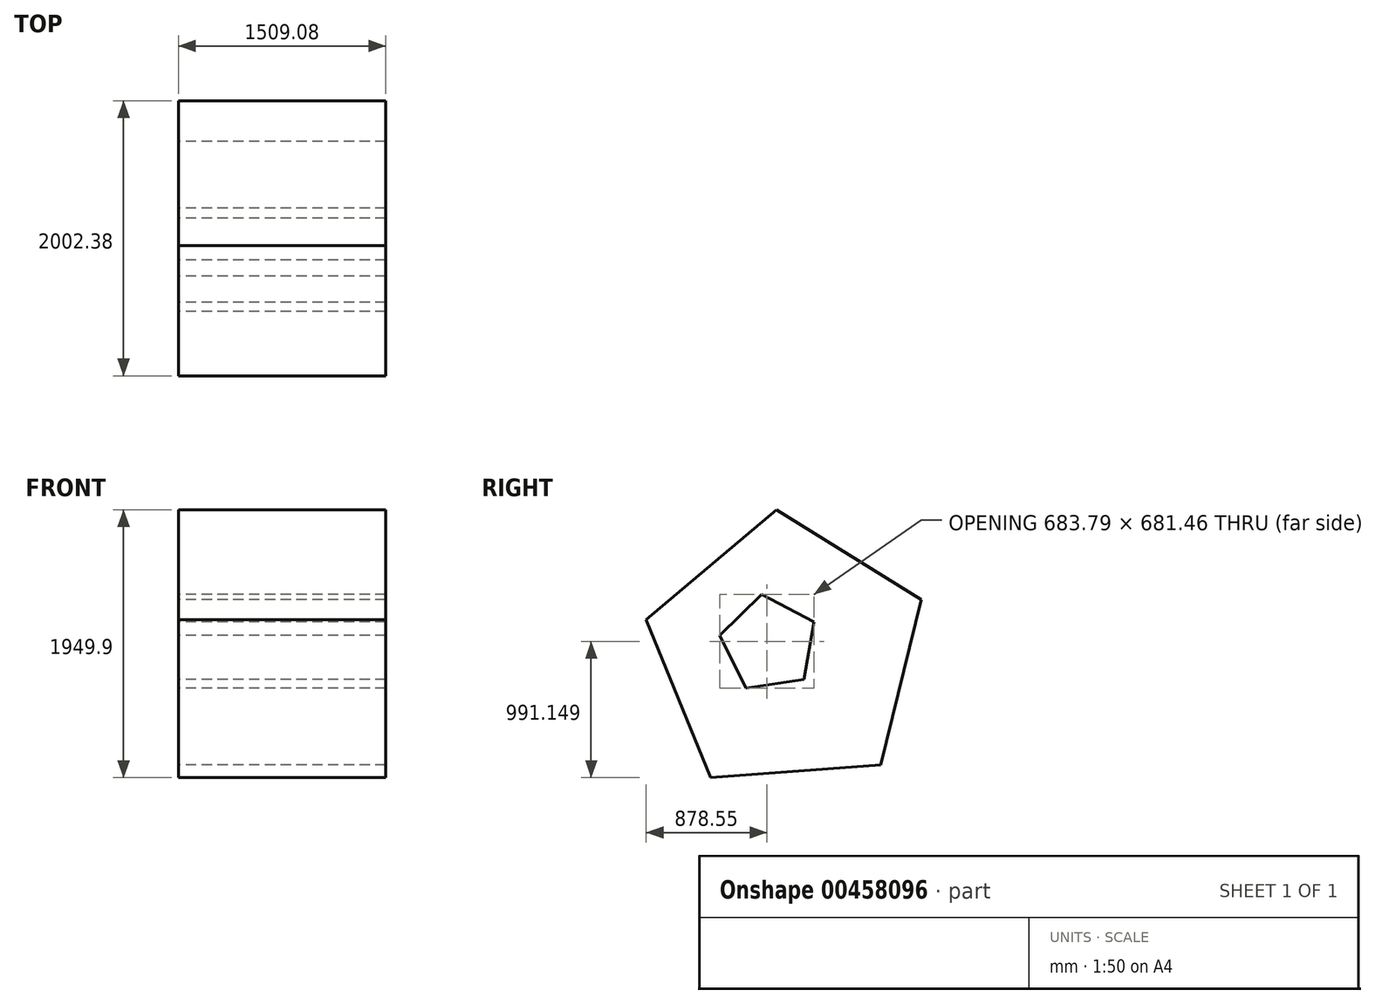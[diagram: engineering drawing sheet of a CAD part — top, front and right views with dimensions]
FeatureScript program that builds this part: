
annotation { "Feature Type Name" : "Feature", "Feature Type Description" : "" }
export const myFeature = defineFeature(function(context is Context, id is Id, definition is map)
    precondition{}
    {
        {
            var Q0;
            Q0=qCreatedBy(makeId("Right.planeOp"),FACE);
            var sketch = newSketch(context, id + "F0", { "sketchPlane" : qUnion([Q0])});
            skCircle(sketch, "E0.cCircle", {"center": v(0, 0) * mm, "radius": 105.76 * mm, "construction": true});
            skLineSegment(sketch, "E0.0", {"start": v(-72.68, -76.82) * mm, "end": v(-102.87, 24.53) * mm});
            skLineSegment(sketch, "E0.1", {"start": v(-102.87, 24.53) * mm, "end": v(-30.2, 101.36) * mm});
            skLineSegment(sketch, "E0.2", {"start": v(-30.2, 101.36) * mm, "end": v(72.68, 76.82) * mm});
            skLineSegment(sketch, "E0.3", {"start": v(72.68, 76.82) * mm, "end": v(102.87, -24.53) * mm});
            skLineSegment(sketch, "E0.4", {"start": v(102.87, -24.53) * mm, "end": v(30.2, -101.36) * mm});
            skLineSegment(sketch, "E0.5", {"start": v(30.2, -101.36) * mm, "end": v(-72.68, -76.82) * mm});
            skCircle(sketch, "E1.cCircle", {"center": v(0, 0) * mm, "radius": 363.37 * mm, "construction": true});
            skLineSegment(sketch, "E1.0", {"start": v(-358.27, 60.7) * mm, "end": v(-52.98, 359.5) * mm});
            skLineSegment(sketch, "E1.1", {"start": v(-52.98, 359.5) * mm, "end": v(325.53, 161.47) * mm});
            skLineSegment(sketch, "E1.2", {"start": v(325.53, 161.47) * mm, "end": v(254.16, -259.7) * mm});
            skLineSegment(sketch, "E1.3", {"start": v(254.16, -259.7) * mm, "end": v(-168.45, -321.97) * mm});
            skLineSegment(sketch, "E1.4", {"start": v(-168.45, -321.97) * mm, "end": v(-358.27, 60.7) * mm});
            skCircle(sketch, "E2.cCircle", {"center": v(130.2, -75.2) * mm, "radius": 1055.56 * mm, "construction": true});
            skLineSegment(sketch, "E2.0", {"start": v(-894.92, 176.45) * mm, "end": v(52.75, 977.51) * mm});
            skLineSegment(sketch, "E2.1", {"start": v(52.75, 977.51) * mm, "end": v(1107.46, 323.76) * mm});
            skLineSegment(sketch, "E2.2", {"start": v(1107.46, 323.76) * mm, "end": v(811.63, -881.34) * mm});
            skLineSegment(sketch, "E2.3", {"start": v(811.63, -881.34) * mm, "end": v(-425.91, -972.4) * mm});
            skLineSegment(sketch, "E2.4", {"start": v(-425.91, -972.4) * mm, "end": v(-894.92, 176.45) * mm});
            skSolve(sketch);
        }
        {
            var Q0;
            Q0 = qSketchRegion(id + "F0", true);
            extrude(context, id + "F1", {"entities" : qUnion([Q0]), "depth" : 25.4 * mm});
        }
        {
            var Q0;
            Q0=makeQuery(id+"F1.opExtrude","CAP_FACE",FACE,{"disambiguationData":[OSD([sQuery(id+"F0.wireOp",EDGE,"E1.0"),sQuery(id+"F0.wireOp",EDGE,"E1.1"),sQuery(id+"F0.wireOp",EDGE,"E1.2"),sQuery(id+"F0.wireOp",EDGE,"E1.3"),sQuery(id+"F0.wireOp",EDGE,"E1.4"),sQuery(id+"F0.wireOp",EDGE,"E2.0"),sQuery(id+"F0.wireOp",EDGE,"E2.1"),sQuery(id+"F0.wireOp",EDGE,"E2.2"),sQuery(id+"F0.wireOp",EDGE,"E2.3"),sQuery(id+"F0.wireOp",EDGE,"E2.4")])],"isStart":true});
            extrude(context, id + "F2", {"entities" : qUnion([Q0]), "operationType" : NewBodyOperationType.ADD, "depth" : 1483.68 * mm});
        }
    });
